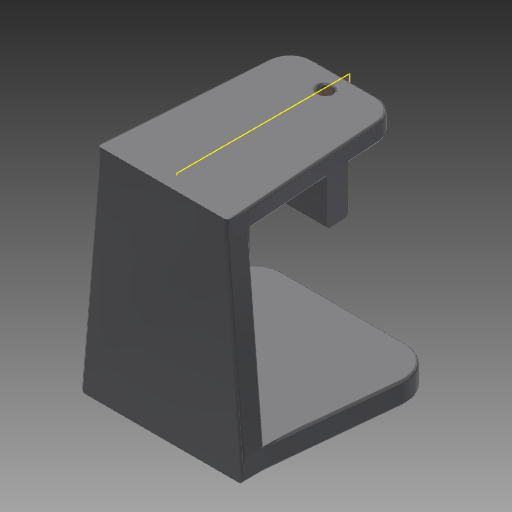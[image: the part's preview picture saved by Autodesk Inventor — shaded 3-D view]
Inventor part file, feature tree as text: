
AUTODESK INVENTOR PART (.ipt)
format: ipt  version: 2017.1 (Build 211199000, 199)  size: 284,672 bytes
history: native  units: mm
features: extrude x4, sketch x4, projected_geometry x3, fillet x2, plane x1
ambient origin geometry x8: Origin, YZ Plane, XZ Plane, XY Plane, X Axis, Y Axis, Z Axis, Center Point
bodies: Solid1 (feature_tree)
feature tree (14):
  extrude  "Extrusion1"  Depth=10.0mm
  plane  "Work Plane1"
  extrude  "Extrusion2"  Depth=10.0mm
  extrude  "Extrusion3"  Depth=10.0mm TaperAngle=0.0deg
  extrude  "Extrusion4"  Depth=0.5mm
  fillet  "Fillet2"  Radius=3.5mm
  fillet  "Fillet5"  Radius=30.0mm
  sketch  "Sketch1"  dims[d0=3.0mm d1=0.0mm d3=10.0mm]
  sketch  "Sketch3"  dims[d4=5.0mm d6=10.0mm]
  sketch  "Sketch5"  dims[d7=3.5mm d8=10.0mm d9=0.0mm]
  sketch  "Sketch6"  dims[d10=28.0mm d11=25.0mm d12=3.5mm d13=0.0mm d14=30.0mm d15=15.0mm d16=25.0mm d17=3.5mm d18=0.0mm d19=5.0mm d22=0.5mm]
  projected_geometry  "Project Cut Edges1"
  projected_geometry  "Project Cut Edges2"
  projected_geometry  "Project Cut Edges3"
